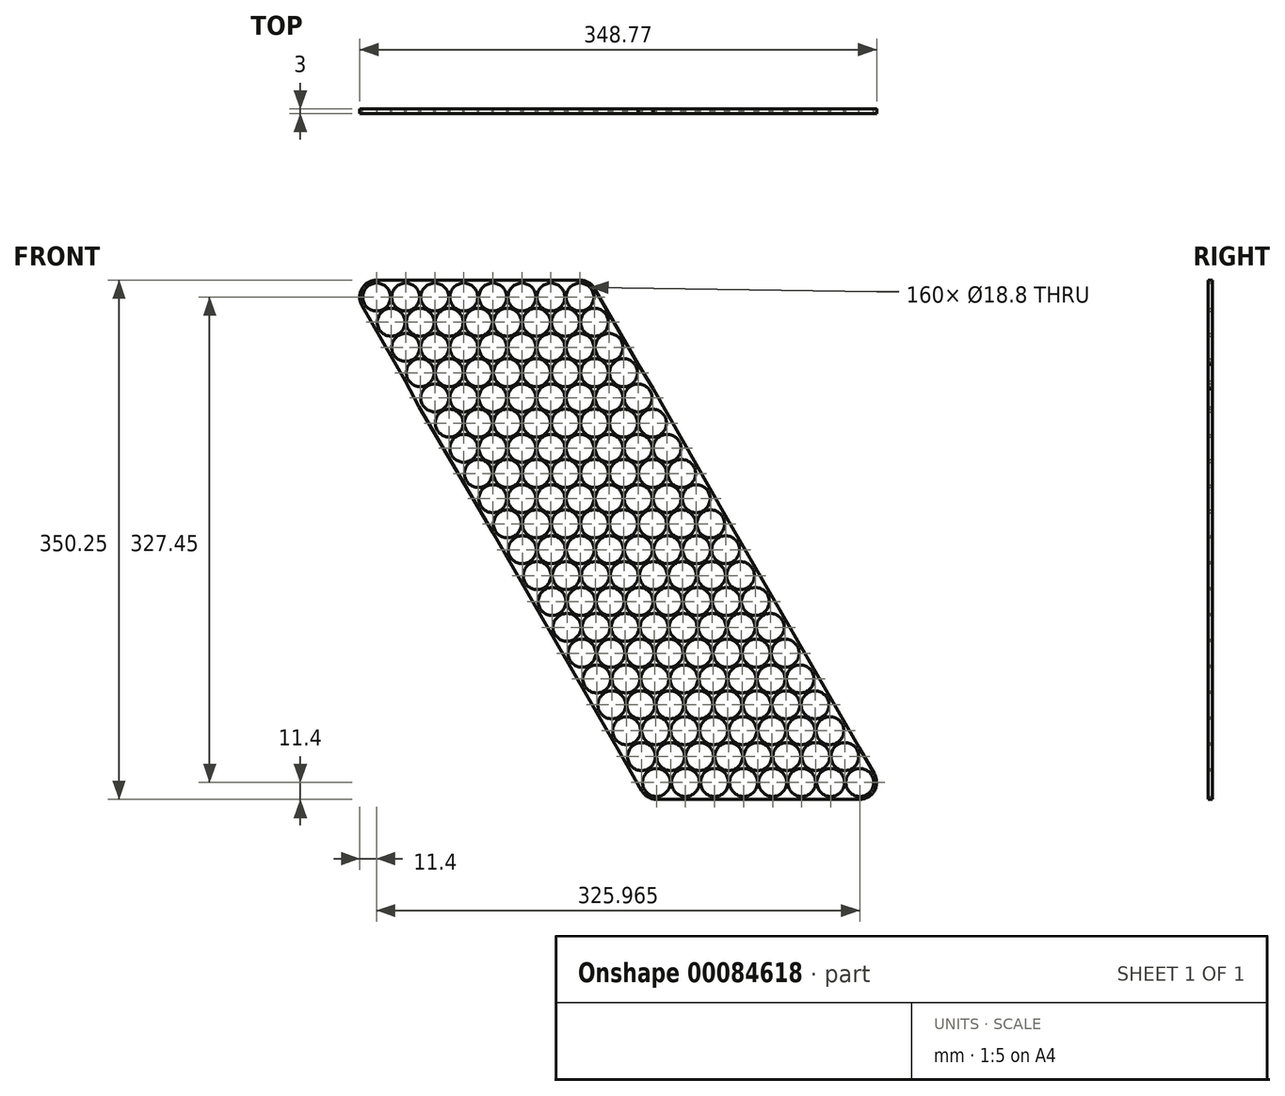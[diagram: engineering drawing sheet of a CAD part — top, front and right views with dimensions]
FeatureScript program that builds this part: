
annotation { "Feature Type Name" : "Feature", "Feature Type Description" : "" }
export const myFeature = defineFeature(function(context is Context, id is Id, definition is map)
    precondition{}
    {
        {
            var Q0;
            Q0=qCreatedBy(makeId("Front.planeOp"),FACE);
            var sketch = newSketch(context, id + "F0", { "sketchPlane" : qUnion([Q0]) });
            skCircle(sketch, "E0", {"center": v(0, 0) * mm, "radius": 9.4 * mm});
            skCircle(sketch, "E1.1.0.0", {"center": v(19.6, 0) * mm, "radius": 9.4 * mm});
            skCircle(sketch, "E1.2.0.0", {"center": v(39.2, 0) * mm, "radius": 9.4 * mm});
            skCircle(sketch, "E1.3.0.0", {"center": v(58.8, 0) * mm, "radius": 9.4 * mm});
            skLineSegment(sketch, "E1.direction1", {"start": v(0, 0) * mm, "end": v(19.6, 0) * mm, "construction": true});
            skLineSegment(sketch, "E2", {"start": v(0, -17) * mm, "end": v(73.2, -17) * mm, "construction": true});
            skLineSegment(sketch, "E3", {"start": v(9.8, 0) * mm, "end": v(9.8, -17) * mm, "construction": true});
            skCircle(sketch, "E4", {"center": v(9.8, -17) * mm, "radius": 9.4 * mm});
            skCircle(sketch, "E5.1.0.0", {"center": v(29.4, -17) * mm, "radius": 9.4 * mm});
            skCircle(sketch, "E5.2.0.0", {"center": v(49, -17) * mm, "radius": 9.4 * mm});
            skCircle(sketch, "E5.3.0.0", {"center": v(68.6, -17) * mm, "radius": 9.4 * mm});
            skLineSegment(sketch, "E5.direction1", {"start": v(9.8, -17) * mm, "end": v(29.4, -17) * mm, "construction": true});
            skLineSegment(sketch, "E6", {"start": v(-8.14, -4.7) * mm, "end": v(1.66, -21.7) * mm});
            skLineSegment(sketch, "E7", {"start": v(0, 9.4) * mm, "end": v(58.8, 9.4) * mm});
            skLineSegment(sketch, "E8", {"start": v(9.8, -17) * mm, "end": v(9.8, -26.4) * mm, "construction": true});
            skLineSegment(sketch, "E9", {"start": v(68.6, -17) * mm, "end": v(68.6, -26.4) * mm, "construction": true});
            skArc(sketch, "E10", {"start": v(58.8, 9.4) * mm, "mid": v(63.5, 8.14) * mm, "end": v(66.94, 4.7) * mm});
            skArc(sketch, "E11", {"start": v(76.74, -12.3) * mm, "mid": v(76.74, -21.7) * mm, "end": v(68.6, -26.4) * mm});
            skArc(sketch, "E12", {"start": v(9.8, -26.4) * mm, "mid": v(5.1, -25.14) * mm, "end": v(1.66, -21.7) * mm});
            skArc(sketch, "E13", {"start": v(-8.14, -4.7) * mm, "mid": v(-8.14, 4.7) * mm, "end": v(0, 9.4) * mm});
            skArc(sketch, "E14.0", {"start": v(0, 11.4) * mm, "mid": v(-9.87, 5.7) * mm, "end": v(-9.88, -5.7) * mm});
            skLineSegment(sketch, "E15.0", {"start": v(0, 11.4) * mm, "end": v(58.8, 11.4) * mm});
            skLineSegment(sketch, "E16.0", {"start": v(-9.88, -5.7) * mm, "end": v(-0.08, -22.7) * mm});
            skArc(sketch, "E17.trimOffspring", {"start": v(9.8, -5.82) * mm, "mid": v(9.87, -5.71) * mm, "end": v(9.93, -5.6) * mm});
            skArc(sketch, "E18.trimOffspring", {"start": v(9.93, -5.6) * mm, "mid": v(9.86, -5.6) * mm, "end": v(9.8, -5.6) * mm});
            skCircle(sketch, "E19.0.4.0", {"center": v(78.4, 0) * mm, "radius": 9.4 * mm});
            skCircle(sketch, "E19.0.5.0", {"center": v(98, 0) * mm, "radius": 9.4 * mm});
            skCircle(sketch, "E20.0.4.0", {"center": v(88.2, -17) * mm, "radius": 9.4 * mm});
            skCircle(sketch, "E20.0.5.0", {"center": v(107.8, -17) * mm, "radius": 9.4 * mm});
            skLineSegment(sketch, "E21", {"start": v(58.8, 11.4) * mm, "end": v(98, 11.4) * mm});
            skLineSegment(sketch, "E22", {"start": v(0, 0) * mm, "end": v(9.8, -17) * mm, "construction": true});
            skCircle(sketch, "E23.1.0.0", {"center": v(19.6, -34) * mm, "radius": 9.4 * mm});
            skCircle(sketch, "E23.2.0.0", {"center": v(29.4, -51) * mm, "radius": 9.4 * mm});
            skLineSegment(sketch, "E23.direction1", {"start": v(9.8, -17) * mm, "end": v(19.6, -34) * mm, "construction": true});
            skCircle(sketch, "E24.1.0.0", {"center": v(39.2, -34) * mm, "radius": 9.4 * mm});
            skCircle(sketch, "E24.1.0.1", {"center": v(49, -51) * mm, "radius": 9.4 * mm});
            skCircle(sketch, "E24.2.0.0", {"center": v(58.8, -34) * mm, "radius": 9.4 * mm});
            skCircle(sketch, "E24.2.0.1", {"center": v(68.6, -51) * mm, "radius": 9.4 * mm});
            skCircle(sketch, "E24.3.0.0", {"center": v(78.4, -34) * mm, "radius": 9.4 * mm});
            skCircle(sketch, "E24.3.0.1", {"center": v(88.2, -51) * mm, "radius": 9.4 * mm});
            skCircle(sketch, "E24.4.0.0", {"center": v(98, -34) * mm, "radius": 9.4 * mm});
            skCircle(sketch, "E24.4.0.1", {"center": v(107.8, -51) * mm, "radius": 9.4 * mm});
            skCircle(sketch, "E24.5.0.0", {"center": v(117.6, -34) * mm, "radius": 9.4 * mm});
            skCircle(sketch, "E24.5.0.1", {"center": v(127.4, -51) * mm, "radius": 9.4 * mm});
            skLineSegment(sketch, "E24.direction1", {"start": v(19.6, -34) * mm, "end": v(39.2, -34) * mm, "construction": true});
            skLineSegment(sketch, "E25", {"start": v(-0.08, -22.7) * mm, "end": v(19.52, -56.7) * mm});
            skArc(sketch, "E26.0", {"start": v(29.27, -62.4) * mm, "mid": v(29.33, -62.4) * mm, "end": v(29.4, -62.4) * mm});
            skCircle(sketch, "E27.0.6.0", {"center": v(117.6, 0) * mm, "radius": 9.4 * mm});
            skCircle(sketch, "E27.0.7.0", {"center": v(137.2, 0) * mm, "radius": 9.4 * mm});
            skCircle(sketch, "E28.0.6.0", {"center": v(127.4, -17) * mm, "radius": 9.4 * mm});
            skCircle(sketch, "E28.0.7.0", {"center": v(147, -17) * mm, "radius": 9.4 * mm});
            skCircle(sketch, "E29.0.6.0", {"center": v(137.2, -34) * mm, "radius": 9.4 * mm});
            skCircle(sketch, "E29.2.6.0", {"center": v(147, -51) * mm, "radius": 9.4 * mm});
            skCircle(sketch, "E29.0.7.0", {"center": v(156.8, -34) * mm, "radius": 9.4 * mm});
            skCircle(sketch, "E29.2.7.0", {"center": v(166.6, -51) * mm, "radius": 9.4 * mm});
            skArc(sketch, "E30.0", {"start": v(147.08, 5.7) * mm, "mid": v(142.9, 9.87) * mm, "end": v(137.2, 11.4) * mm});
            skLineSegment(sketch, "E31", {"start": v(98, 11.4) * mm, "end": v(137.2, 11.4) * mm});
            skLineSegment(sketch, "E32", {"start": v(147.08, 5.7) * mm, "end": v(176.48, -45.3) * mm});
            skCircle(sketch, "E33.0.3.0", {"center": v(39.2, -68) * mm, "radius": 9.4 * mm});
            skCircle(sketch, "E34.1.0.0", {"center": v(58.8, -68) * mm, "radius": 9.4 * mm});
            skCircle(sketch, "E34.2.0.0", {"center": v(78.4, -68) * mm, "radius": 9.4 * mm});
            skCircle(sketch, "E34.3.0.0", {"center": v(98, -68) * mm, "radius": 9.4 * mm});
            skCircle(sketch, "E34.4.0.0", {"center": v(117.6, -68) * mm, "radius": 9.4 * mm});
            skCircle(sketch, "E34.5.0.0", {"center": v(137.2, -68) * mm, "radius": 9.4 * mm});
            skCircle(sketch, "E34.6.0.0", {"center": v(156.8, -68) * mm, "radius": 9.4 * mm});
            skCircle(sketch, "E34.7.0.0", {"center": v(176.4, -68) * mm, "radius": 9.4 * mm});
            skLineSegment(sketch, "E34.direction1", {"start": v(39.2, -68) * mm, "end": v(58.8, -68) * mm, "construction": true});
            skLineSegment(sketch, "E35", {"start": v(19.52, -56.7) * mm, "end": v(28.57, -74.14) * mm});
            skLineSegment(sketch, "E36", {"start": v(176.48, -45.3) * mm, "end": v(186.68, -62.07) * mm});
            skCircle(sketch, "E37.1.0.0", {"center": v(49, -85) * mm, "radius": 9.4 * mm});
            skCircle(sketch, "E37.1.0.1", {"center": v(68.6, -85) * mm, "radius": 9.4 * mm});
            skCircle(sketch, "E37.1.0.2", {"center": v(88.2, -85) * mm, "radius": 9.4 * mm});
            skCircle(sketch, "E37.1.0.3", {"center": v(107.8, -85) * mm, "radius": 9.4 * mm});
            skCircle(sketch, "E37.1.0.4", {"center": v(127.4, -85) * mm, "radius": 9.4 * mm});
            skCircle(sketch, "E37.1.0.5", {"center": v(147, -85) * mm, "radius": 9.4 * mm});
            skCircle(sketch, "E37.1.0.6", {"center": v(166.6, -85) * mm, "radius": 9.4 * mm});
            skCircle(sketch, "E37.1.0.7", {"center": v(186.2, -85) * mm, "radius": 9.4 * mm});
            skCircle(sketch, "E37.2.0.0", {"center": v(58.8, -102) * mm, "radius": 9.4 * mm});
            skCircle(sketch, "E37.2.0.1", {"center": v(78.4, -102) * mm, "radius": 9.4 * mm});
            skCircle(sketch, "E37.2.0.2", {"center": v(98, -102) * mm, "radius": 9.4 * mm});
            skCircle(sketch, "E37.2.0.3", {"center": v(117.6, -102) * mm, "radius": 9.4 * mm});
            skCircle(sketch, "E37.2.0.4", {"center": v(137.2, -102) * mm, "radius": 9.4 * mm});
            skCircle(sketch, "E37.2.0.5", {"center": v(156.8, -102) * mm, "radius": 9.4 * mm});
            skCircle(sketch, "E37.2.0.6", {"center": v(176.4, -102) * mm, "radius": 9.4 * mm});
            skCircle(sketch, "E37.2.0.7", {"center": v(196, -102) * mm, "radius": 9.4 * mm});
            skCircle(sketch, "E37.3.0.0", {"center": v(68.6, -119) * mm, "radius": 9.4 * mm});
            skCircle(sketch, "E37.3.0.1", {"center": v(88.2, -119) * mm, "radius": 9.4 * mm});
            skCircle(sketch, "E37.3.0.2", {"center": v(107.8, -119) * mm, "radius": 9.4 * mm});
            skCircle(sketch, "E37.3.0.3", {"center": v(127.4, -119) * mm, "radius": 9.4 * mm});
            skCircle(sketch, "E37.3.0.4", {"center": v(147, -119) * mm, "radius": 9.4 * mm});
            skCircle(sketch, "E37.3.0.5", {"center": v(166.6, -119) * mm, "radius": 9.4 * mm});
            skCircle(sketch, "E37.3.0.6", {"center": v(186.2, -119) * mm, "radius": 9.4 * mm});
            skCircle(sketch, "E37.3.0.7", {"center": v(205.8, -119) * mm, "radius": 9.4 * mm});
            skCircle(sketch, "E37.4.0.0", {"center": v(78.4, -136) * mm, "radius": 9.4 * mm});
            skCircle(sketch, "E37.4.0.1", {"center": v(98, -136) * mm, "radius": 9.4 * mm});
            skCircle(sketch, "E37.4.0.2", {"center": v(117.6, -136) * mm, "radius": 9.4 * mm});
            skCircle(sketch, "E37.4.0.3", {"center": v(137.2, -136) * mm, "radius": 9.4 * mm});
            skCircle(sketch, "E37.4.0.4", {"center": v(156.8, -136) * mm, "radius": 9.4 * mm});
            skCircle(sketch, "E37.4.0.5", {"center": v(176.4, -136) * mm, "radius": 9.4 * mm});
            skCircle(sketch, "E37.4.0.6", {"center": v(196, -136) * mm, "radius": 9.4 * mm});
            skCircle(sketch, "E37.4.0.7", {"center": v(215.6, -136) * mm, "radius": 9.4 * mm});
            skCircle(sketch, "E37.5.0.0", {"center": v(88.2, -153) * mm, "radius": 9.4 * mm});
            skCircle(sketch, "E37.5.0.1", {"center": v(107.8, -153) * mm, "radius": 9.4 * mm});
            skCircle(sketch, "E37.5.0.2", {"center": v(127.4, -153) * mm, "radius": 9.4 * mm});
            skCircle(sketch, "E37.5.0.3", {"center": v(147, -153) * mm, "radius": 9.4 * mm});
            skCircle(sketch, "E37.5.0.4", {"center": v(166.6, -153) * mm, "radius": 9.4 * mm});
            skCircle(sketch, "E37.5.0.5", {"center": v(186.2, -153) * mm, "radius": 9.4 * mm});
            skCircle(sketch, "E37.5.0.6", {"center": v(205.8, -153) * mm, "radius": 9.4 * mm});
            skCircle(sketch, "E37.5.0.7", {"center": v(225.4, -153) * mm, "radius": 9.4 * mm});
            skLineSegment(sketch, "E37.direction1", {"start": v(39.2, -68) * mm, "end": v(49, -85) * mm, "construction": true});
            skLineSegment(sketch, "E38", {"start": v(28.57, -74.14) * mm, "end": v(78.37, -158.78) * mm});
            skLineSegment(sketch, "E39", {"start": v(186.68, -62.07) * mm, "end": v(235.3, -147.35) * mm});
            skCircle(sketch, "E40.1.0.0", {"center": v(98.25, -170.44) * mm, "radius": 9.4 * mm});
            skCircle(sketch, "E40.1.0.1", {"center": v(117.85, -170.44) * mm, "radius": 9.4 * mm});
            skCircle(sketch, "E40.1.0.2", {"center": v(137.45, -170.44) * mm, "radius": 9.4 * mm});
            skCircle(sketch, "E40.1.0.3", {"center": v(157.05, -170.44) * mm, "radius": 9.4 * mm});
            skCircle(sketch, "E40.1.0.4", {"center": v(176.65, -170.44) * mm, "radius": 9.4 * mm});
            skCircle(sketch, "E40.1.0.5", {"center": v(196.25, -170.44) * mm, "radius": 9.4 * mm});
            skCircle(sketch, "E40.1.0.6", {"center": v(215.85, -170.44) * mm, "radius": 9.4 * mm});
            skCircle(sketch, "E40.1.0.7", {"center": v(235.45, -170.44) * mm, "radius": 9.4 * mm});
            skCircle(sketch, "E40.2.0.0", {"center": v(108.31, -187.89) * mm, "radius": 9.4 * mm});
            skCircle(sketch, "E40.2.0.1", {"center": v(127.91, -187.89) * mm, "radius": 9.4 * mm});
            skCircle(sketch, "E40.2.0.2", {"center": v(147.51, -187.89) * mm, "radius": 9.4 * mm});
            skCircle(sketch, "E40.2.0.3", {"center": v(167.11, -187.89) * mm, "radius": 9.4 * mm});
            skCircle(sketch, "E40.2.0.4", {"center": v(186.71, -187.89) * mm, "radius": 9.4 * mm});
            skCircle(sketch, "E40.2.0.5", {"center": v(206.31, -187.89) * mm, "radius": 9.4 * mm});
            skCircle(sketch, "E40.2.0.6", {"center": v(225.91, -187.89) * mm, "radius": 9.4 * mm});
            skCircle(sketch, "E40.2.0.7", {"center": v(245.51, -187.89) * mm, "radius": 9.4 * mm});
            skCircle(sketch, "E40.3.0.0", {"center": v(118.37, -205.33) * mm, "radius": 9.4 * mm});
            skCircle(sketch, "E40.3.0.1", {"center": v(137.97, -205.33) * mm, "radius": 9.4 * mm});
            skCircle(sketch, "E40.3.0.2", {"center": v(157.57, -205.33) * mm, "radius": 9.4 * mm});
            skCircle(sketch, "E40.3.0.3", {"center": v(177.17, -205.33) * mm, "radius": 9.4 * mm});
            skCircle(sketch, "E40.3.0.4", {"center": v(196.77, -205.33) * mm, "radius": 9.4 * mm});
            skCircle(sketch, "E40.3.0.5", {"center": v(216.37, -205.33) * mm, "radius": 9.4 * mm});
            skCircle(sketch, "E40.3.0.6", {"center": v(235.97, -205.33) * mm, "radius": 9.4 * mm});
            skCircle(sketch, "E40.3.0.7", {"center": v(255.57, -205.33) * mm, "radius": 9.4 * mm});
            skCircle(sketch, "E40.4.0.0", {"center": v(128.43, -222.78) * mm, "radius": 9.4 * mm});
            skCircle(sketch, "E40.4.0.1", {"center": v(148.03, -222.78) * mm, "radius": 9.4 * mm});
            skCircle(sketch, "E40.4.0.2", {"center": v(167.63, -222.78) * mm, "radius": 9.4 * mm});
            skCircle(sketch, "E40.4.0.3", {"center": v(187.23, -222.78) * mm, "radius": 9.4 * mm});
            skCircle(sketch, "E40.4.0.4", {"center": v(206.83, -222.78) * mm, "radius": 9.4 * mm});
            skCircle(sketch, "E40.4.0.5", {"center": v(226.43, -222.78) * mm, "radius": 9.4 * mm});
            skCircle(sketch, "E40.4.0.6", {"center": v(246.03, -222.78) * mm, "radius": 9.4 * mm});
            skCircle(sketch, "E40.4.0.7", {"center": v(265.63, -222.78) * mm, "radius": 9.4 * mm});
            skCircle(sketch, "E40.5.0.0", {"center": v(138.48, -240.22) * mm, "radius": 9.4 * mm});
            skCircle(sketch, "E40.5.0.1", {"center": v(158.08, -240.22) * mm, "radius": 9.4 * mm});
            skCircle(sketch, "E40.5.0.2", {"center": v(177.68, -240.22) * mm, "radius": 9.4 * mm});
            skCircle(sketch, "E40.5.0.3", {"center": v(197.28, -240.22) * mm, "radius": 9.4 * mm});
            skCircle(sketch, "E40.5.0.4", {"center": v(216.88, -240.22) * mm, "radius": 9.4 * mm});
            skCircle(sketch, "E40.5.0.5", {"center": v(236.48, -240.22) * mm, "radius": 9.4 * mm});
            skCircle(sketch, "E40.5.0.6", {"center": v(256.08, -240.22) * mm, "radius": 9.4 * mm});
            skCircle(sketch, "E40.5.0.7", {"center": v(275.68, -240.22) * mm, "radius": 9.4 * mm});
            skCircle(sketch, "E40.6.0.0", {"center": v(148.54, -257.67) * mm, "radius": 9.4 * mm});
            skCircle(sketch, "E40.6.0.1", {"center": v(168.14, -257.67) * mm, "radius": 9.4 * mm});
            skCircle(sketch, "E40.6.0.2", {"center": v(187.74, -257.67) * mm, "radius": 9.4 * mm});
            skCircle(sketch, "E40.6.0.3", {"center": v(207.34, -257.67) * mm, "radius": 9.4 * mm});
            skCircle(sketch, "E40.6.0.4", {"center": v(226.94, -257.67) * mm, "radius": 9.4 * mm});
            skCircle(sketch, "E40.6.0.5", {"center": v(246.54, -257.67) * mm, "radius": 9.4 * mm});
            skCircle(sketch, "E40.6.0.6", {"center": v(266.14, -257.67) * mm, "radius": 9.4 * mm});
            skCircle(sketch, "E40.6.0.7", {"center": v(285.74, -257.67) * mm, "radius": 9.4 * mm});
            skCircle(sketch, "E40.7.0.0", {"center": v(158.6, -275.11) * mm, "radius": 9.4 * mm});
            skCircle(sketch, "E40.7.0.1", {"center": v(178.2, -275.11) * mm, "radius": 9.4 * mm});
            skCircle(sketch, "E40.7.0.2", {"center": v(197.8, -275.11) * mm, "radius": 9.4 * mm});
            skCircle(sketch, "E40.7.0.3", {"center": v(217.4, -275.11) * mm, "radius": 9.4 * mm});
            skCircle(sketch, "E40.7.0.4", {"center": v(237, -275.11) * mm, "radius": 9.4 * mm});
            skCircle(sketch, "E40.7.0.5", {"center": v(256.6, -275.11) * mm, "radius": 9.4 * mm});
            skCircle(sketch, "E40.7.0.6", {"center": v(276.2, -275.11) * mm, "radius": 9.4 * mm});
            skCircle(sketch, "E40.7.0.7", {"center": v(295.8, -275.11) * mm, "radius": 9.4 * mm});
            skCircle(sketch, "E40.8.0.0", {"center": v(168.65, -292.56) * mm, "radius": 9.4 * mm});
            skCircle(sketch, "E40.8.0.1", {"center": v(188.25, -292.56) * mm, "radius": 9.4 * mm});
            skCircle(sketch, "E40.8.0.2", {"center": v(207.85, -292.56) * mm, "radius": 9.4 * mm});
            skCircle(sketch, "E40.8.0.3", {"center": v(227.45, -292.56) * mm, "radius": 9.4 * mm});
            skCircle(sketch, "E40.8.0.4", {"center": v(247.05, -292.56) * mm, "radius": 9.4 * mm});
            skCircle(sketch, "E40.8.0.5", {"center": v(266.65, -292.56) * mm, "radius": 9.4 * mm});
            skCircle(sketch, "E40.8.0.6", {"center": v(286.25, -292.56) * mm, "radius": 9.4 * mm});
            skCircle(sketch, "E40.8.0.7", {"center": v(305.85, -292.56) * mm, "radius": 9.4 * mm});
            skCircle(sketch, "E40.9.0.0", {"center": v(178.7, -310) * mm, "radius": 9.4 * mm});
            skCircle(sketch, "E40.9.0.1", {"center": v(198.3, -310) * mm, "radius": 9.4 * mm});
            skCircle(sketch, "E40.9.0.2", {"center": v(217.9, -310) * mm, "radius": 9.4 * mm});
            skCircle(sketch, "E40.9.0.3", {"center": v(237.5, -310) * mm, "radius": 9.4 * mm});
            skCircle(sketch, "E40.9.0.4", {"center": v(257.1, -310) * mm, "radius": 9.4 * mm});
            skCircle(sketch, "E40.9.0.5", {"center": v(276.7, -310) * mm, "radius": 9.4 * mm});
            skCircle(sketch, "E40.9.0.6", {"center": v(296.3, -310) * mm, "radius": 9.4 * mm});
            skCircle(sketch, "E40.9.0.7", {"center": v(315.9, -310) * mm, "radius": 9.4 * mm});
            skLineSegment(sketch, "E40.direction1", {"start": v(88.2, -153) * mm, "end": v(98.25, -170.44) * mm, "construction": true});
            skLineSegment(sketch, "E41.0", {"start": v(168.83, -315.7) * mm, "end": v(168.83, -315.7) * mm});
            skLineSegment(sketch, "E42", {"start": v(235.3, -147.35) * mm, "end": v(325.79, -304.31) * mm});
            skLineSegment(sketch, "E43", {"start": v(78.37, -158.78) * mm, "end": v(168.83, -315.7) * mm});
            skCircle(sketch, "E44.0.10.0", {"center": v(188.77, -327.45) * mm, "radius": 9.4 * mm});
            skCircle(sketch, "E44.2.10.0", {"center": v(208.37, -327.45) * mm, "radius": 9.4 * mm});
            skCircle(sketch, "E44.4.10.0", {"center": v(227.97, -327.45) * mm, "radius": 9.4 * mm});
            skCircle(sketch, "E44.6.10.0", {"center": v(247.57, -327.45) * mm, "radius": 9.4 * mm});
            skCircle(sketch, "E44.8.10.0", {"center": v(267.17, -327.45) * mm, "radius": 9.4 * mm});
            skCircle(sketch, "E44.10.10.0", {"center": v(286.77, -327.45) * mm, "radius": 9.4 * mm});
            skCircle(sketch, "E44.12.10.0", {"center": v(306.37, -327.45) * mm, "radius": 9.4 * mm});
            skCircle(sketch, "E44.14.10.0", {"center": v(325.97, -327.45) * mm, "radius": 9.4 * mm});
            skArc(sketch, "E45.0", {"start": v(178.89, -333.14) * mm, "mid": v(183.06, -337.32) * mm, "end": v(188.77, -338.85) * mm});
            skArc(sketch, "E46.0", {"start": v(325.97, -338.85) * mm, "mid": v(335.84, -333.15) * mm, "end": v(335.84, -321.76) * mm});
            skLineSegment(sketch, "E47", {"start": v(168.83, -315.7) * mm, "end": v(178.89, -333.14) * mm});
            skLineSegment(sketch, "E48", {"start": v(325.79, -304.31) * mm, "end": v(335.84, -321.76) * mm});
            skLineSegment(sketch, "E49", {"start": v(188.77, -338.85) * mm, "end": v(325.97, -338.85) * mm});
            skLineSegment(sketch, "E50.trimOffspring", {"start": v(325.79, -304.31) * mm, "end": v(325.79, -304.31) * mm});
            skSolve(sketch);
        }
        {
            var Q0;
            Q0=makeQuery(id+"F0.imprint","IMPRINT",FACE,{"disambiguationData":[TD([[makeQuery(id+"F0.imprint","IMPRINT",EDGE,{"derivedFrom":sQuery(id+"F0.wireOp",EDGE,"E1.1.0.0")}),-1.0]])]});
            extrude(context, id + "F1", {"entities" : qUnion([Q0]), "depth" : 3 * mm});
        }
    });
